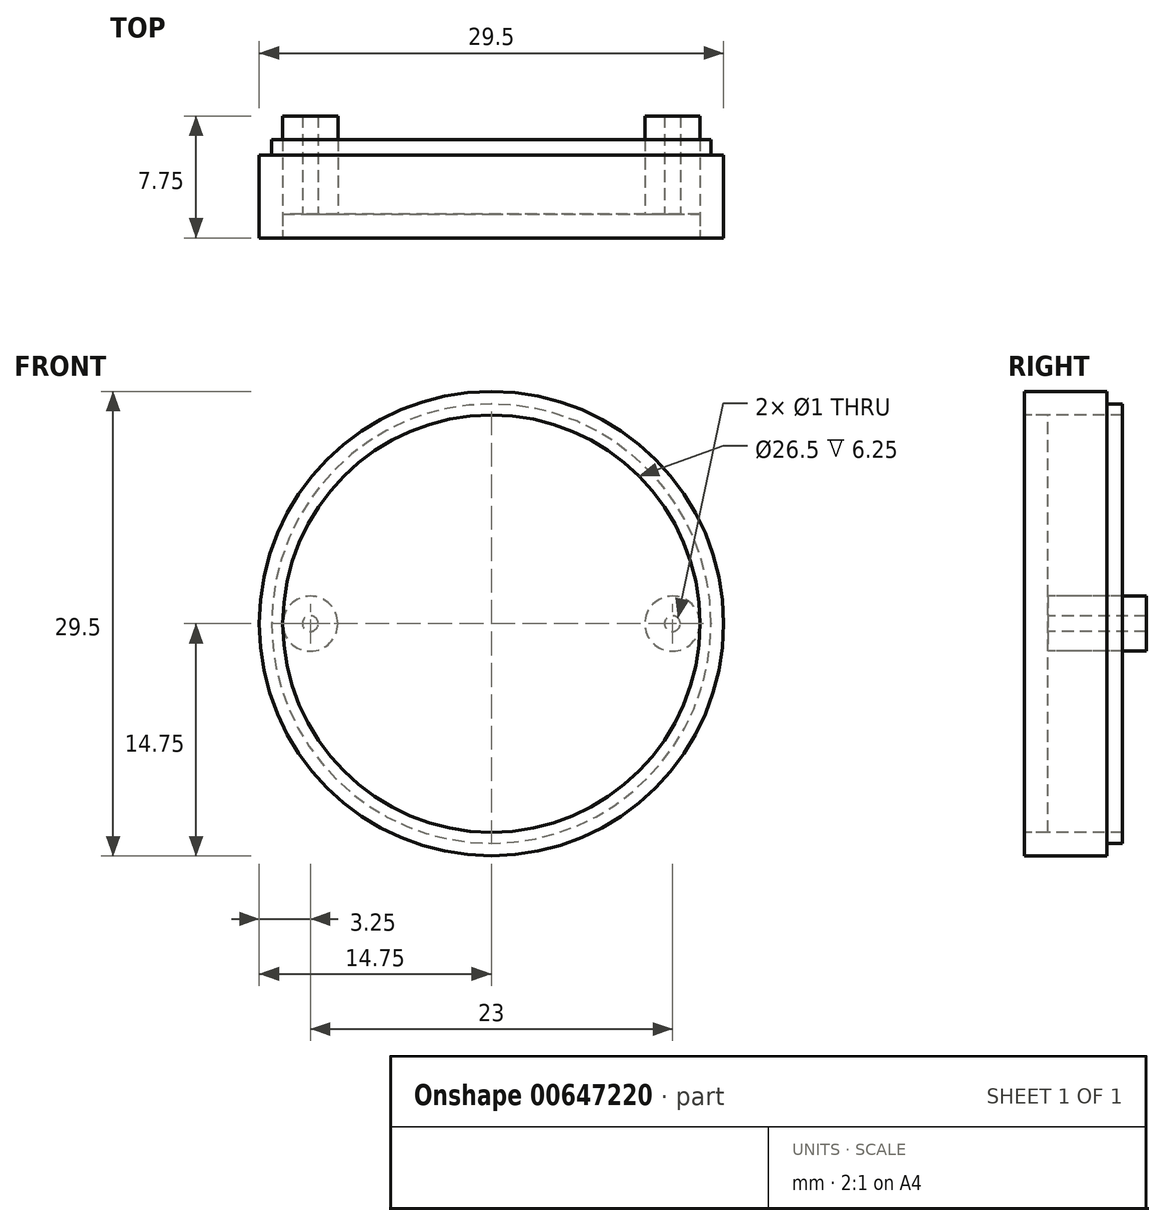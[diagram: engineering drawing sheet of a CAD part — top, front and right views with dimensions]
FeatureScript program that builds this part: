
annotation { "Feature Type Name" : "Feature", "Feature Type Description" : "" }
export const myFeature = defineFeature(function(context is Context, id is Id, definition is map)
    precondition{}
    {
        {
            var Q0;
            Q0=qCreatedBy(makeId("Front.planeOp"),FACE);
            var sketch = newSketch(context, id + "F0", { "sketchPlane" : qUnion([Q0])});
            skCircle(sketch, "E0", {"center": v(0, 0) * mm, "radius": 14.75 * mm});
            skCircle(sketch, "E1", {"center": v(0, 0) * mm, "radius": 13.25 * mm});
            skSolve(sketch);
        }
        {
            var Q0;
            Q0=makeQuery(id+"F0.imprint","IMPRINT",FACE,{"disambiguationData":[TD([[makeQuery(id+"F0.imprint","IMPRINT",EDGE,{"derivedFrom":sQuery(id+"F0.wireOp",EDGE,"E0")}),1.0]])]});
            extrude(context, id + "F1", {"entities" : qUnion([Q0]), "oppositeDirection" : true, "depth" : 6.25 * mm, "offsetDistance" : 25 * mm});
        }
        {
            var Q0;
            Q0=makeQuery(id+"F0.imprint","IMPRINT",FACE,{"disambiguationData":[TD([[makeQuery(id+"F0.imprint","IMPRINT",EDGE,{"derivedFrom":sQuery(id+"F0.wireOp",EDGE,"E1")}),1.0]])]});
            extrude(context, id + "F2", {"entities" : qUnion([Q0]), "oppositeDirection" : true, "depth" : 1.5 * mm, "offsetDistance" : 25 * mm});
        }
        {
            var Q0;
            Q0=makeQuery(id+"F1.opExtrude","CAP_FACE",FACE,{"disambiguationData":[OSD([sQuery(id+"F0.wireOp",EDGE,"E0"),sQuery(id+"F0.wireOp",EDGE,"E1")])],"isStart":false});
            var sketch = newSketch(context, id + "F3", { "sketchPlane" : qUnion([Q0])});
            skCircle(sketch, "E2", {"center": v(0, 0) * mm, "radius": 14.75 * mm});
            skCircle(sketch, "E3", {"center": v(0, 0) * mm, "radius": 13.95 * mm});
            skSolve(sketch);
        }
        {
            var Q0;
            Q0 = qSketchRegion(id + "F3", true);
            extrude(context, id + "F4", {"entities" : qUnion([Q0]), "operationType" : NewBodyOperationType.REMOVE, "oppositeDirection" : true, "depth" : 1 * mm, "offsetDistance" : 25 * mm});
        }
        {
            var Q0;
            Q0=makeQuery(id+"F2.opExtrude","CAP_FACE",FACE,{"disambiguationData":[OSD([sQuery(id+"F0.wireOp",EDGE,"E1")])],"isStart":false});
            var sketch = newSketch(context, id + "F5", { "sketchPlane" : qUnion([Q0])});
            skCircle(sketch, "E4", {"center": v(-11.5, 0) * mm, "radius": 1.75 * mm});
            skCircle(sketch, "E5", {"center": v(-11.5, 0) * mm, "radius": 0.5 * mm});
            skCircle(sketch, "E6", {"center": v(11.5, 0) * mm, "radius": 1.75 * mm});
            skCircle(sketch, "E7", {"center": v(11.5, 0) * mm, "radius": 0.5 * mm});
            skSolve(sketch);
        }
        {
            var Q0;
            Q0 = qSketchRegion(id + "F5", true);
            extrude(context, id + "F6", {"entities" : qUnion([Q0]), "depth" : 6.25 * mm, "offsetDistance" : 25 * mm});
        }
    });
